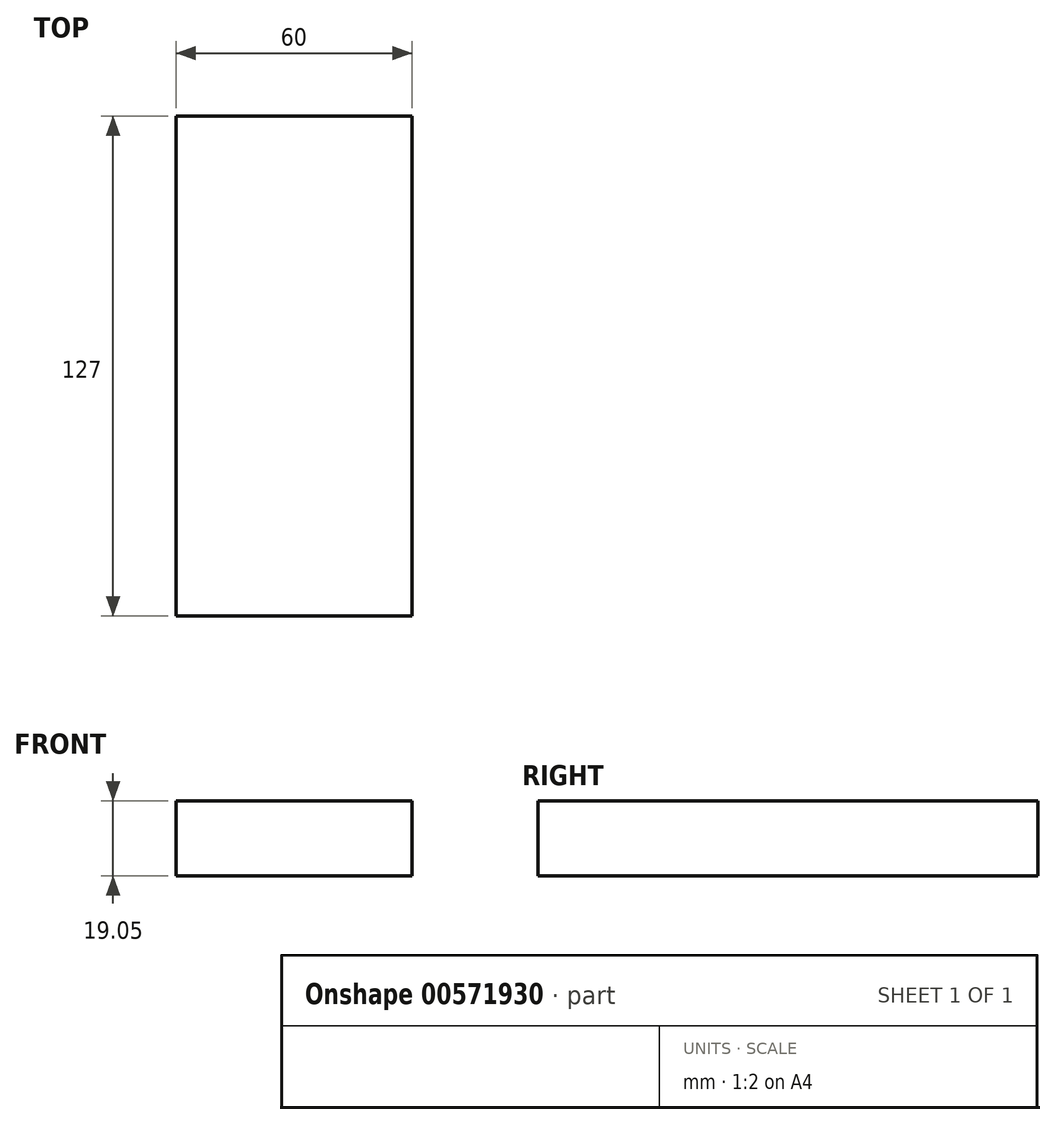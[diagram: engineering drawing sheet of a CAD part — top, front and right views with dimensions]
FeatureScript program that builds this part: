
annotation { "Feature Type Name" : "Feature", "Feature Type Description" : "" }
export const myFeature = defineFeature(function(context is Context, id is Id, definition is map)
    precondition{}
    {
        {
            var Q0;
            Q0=qCreatedBy(makeId("Top.planeOp"),FACE);
            var sketch = newSketch(context, id + "F0", { "sketchPlane" : qUnion([Q0])});
            skLineSegment(sketch, "E0", {"start": v(-60, -67.1) * mm, "end": v(0, -67.1) * mm});
            skLineSegment(sketch, "E1", {"start": v(0, -67.1) * mm, "end": v(0, 59.9) * mm});
            skLineSegment(sketch, "E2", {"start": v(0, 59.9) * mm, "end": v(-60, 59.9) * mm});
            skLineSegment(sketch, "E3", {"start": v(-60, 59.9) * mm, "end": v(-60, -67.1) * mm});
            skSolve(sketch);
        }
        {
            var Q0;
            Q0 = qSketchRegion(id + "F0", true);
            extrude(context, id + "F1", {"entities" : qUnion([Q0]), "depth" : 19.05 * mm, "offsetDistance" : 25.4 * mm});
        }
    });
